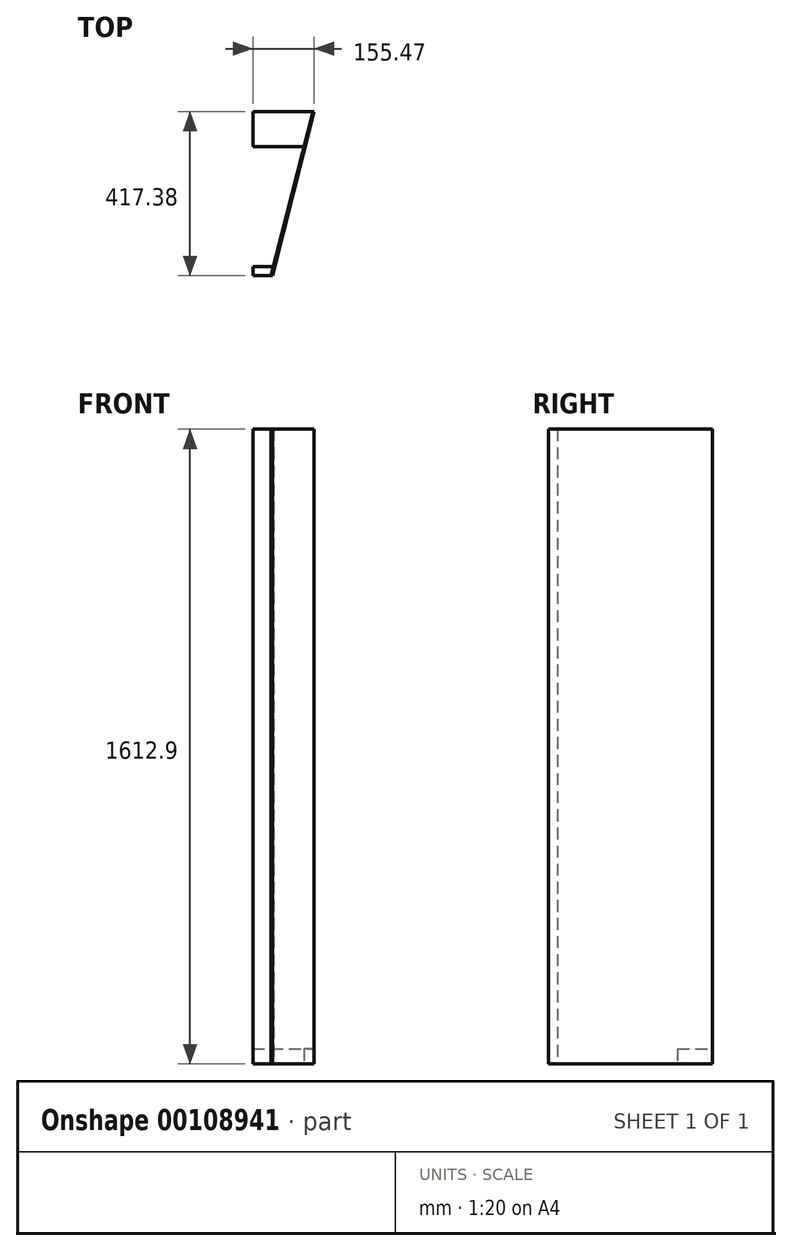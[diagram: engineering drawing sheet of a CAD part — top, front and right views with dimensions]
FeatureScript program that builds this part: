
annotation { "Feature Type Name" : "Feature", "Feature Type Description" : "" }
export const myFeature = defineFeature(function(context is Context, id is Id, definition is map)
    precondition{}
    {
        {
            var Q0;
            Q0=qCreatedBy(makeId("Top.planeOp"),FACE);
            var sketch = newSketch(context, id + "F0", { "sketchPlane" : qUnion([Q0])});
            skLineSegment(sketch, "E0.bottom", {"start": v(-26.2, -11.45) * mm, "end": v(20.37, -11.45) * mm});
            skLineSegment(sketch, "E0.top", {"start": v(-26.2, 11.45) * mm, "end": v(26.2, 11.45) * mm});
            skLineSegment(sketch, "E0.left", {"start": v(-26.2, -11.45) * mm, "end": v(-26.2, 11.45) * mm});
            skPoint(sketch, "E0.middle", {"position": v(0, 0) * mm});
            skLineSegment(sketch, "E1", {"start": v(-26.2, 11.45) * mm, "end": v(-26.2, 316.25) * mm, "construction": true});
            skLineSegment(sketch, "E2.bottom", {"start": v(-26.2, 316.25) * mm, "end": v(103.62, 316.25) * mm});
            skLineSegment(sketch, "E2.top", {"start": v(-26.2, 405.15) * mm, "end": v(126.2, 405.15) * mm});
            skLineSegment(sketch, "E2.left", {"start": v(-26.2, 316.25) * mm, "end": v(-26.2, 405.15) * mm});
            skLineSegment(sketch, "E3", {"start": v(126.2, 405.15) * mm, "end": v(20.37, -11.45) * mm});
            skLineSegment(sketch, "E4.0", {"start": v(129.28, 404.37) * mm, "end": v(23.45, -12.23) * mm});
            skLineSegment(sketch, "E5", {"start": v(126.2, 405.15) * mm, "end": v(129.28, 404.37) * mm});
            skLineSegment(sketch, "E6", {"start": v(23.45, -12.23) * mm, "end": v(20.37, -11.45) * mm});
            skSolve(sketch);
        }
        {
            var Q0;
            {var subQ0=sQuery(id+"F0.wireOp",EDGE,"E0.bottom");Q0=makeQuery(id+"F0.imprint","IMPRINT",FACE,{"disambiguationData":[TD([[makeQuery(id+"F0.imprint","IMPRINT",EDGE,{"derivedFrom":subQ0}),1.0]])]});}
            extrude(context, id + "F1", {"entities" : qUnion([Q0]), "depth" : 1612.9 * mm});
        }
        {
            var Q0;
            {var subQ0=sQuery(id+"F0.wireOp",EDGE,"E2.bottom");Q0=makeQuery(id+"F0.imprint","IMPRINT",FACE,{"disambiguationData":[TD([[makeQuery(id+"F0.imprint","IMPRINT",EDGE,{"derivedFrom":subQ0}),1.0]])]});}
            extrude(context, id + "F2", {"entities" : qUnion([Q0]), "depth" : 38.1 * mm});
        }
        {
            var Q0;
            Q0=makeQuery(id+"F0.imprint","IMPRINT",FACE,{"disambiguationData":[TD([[makeQuery(id+"F0.imprint","IMPRINT",EDGE,{"derivedFrom":sQuery(id+"F0.wireOp",EDGE,"E4.0")}),-1.0]])]});
            extrude(context, id + "F3", {"entities" : qUnion([Q0]), "depth" : 1612.9 * mm});
        }
    });
